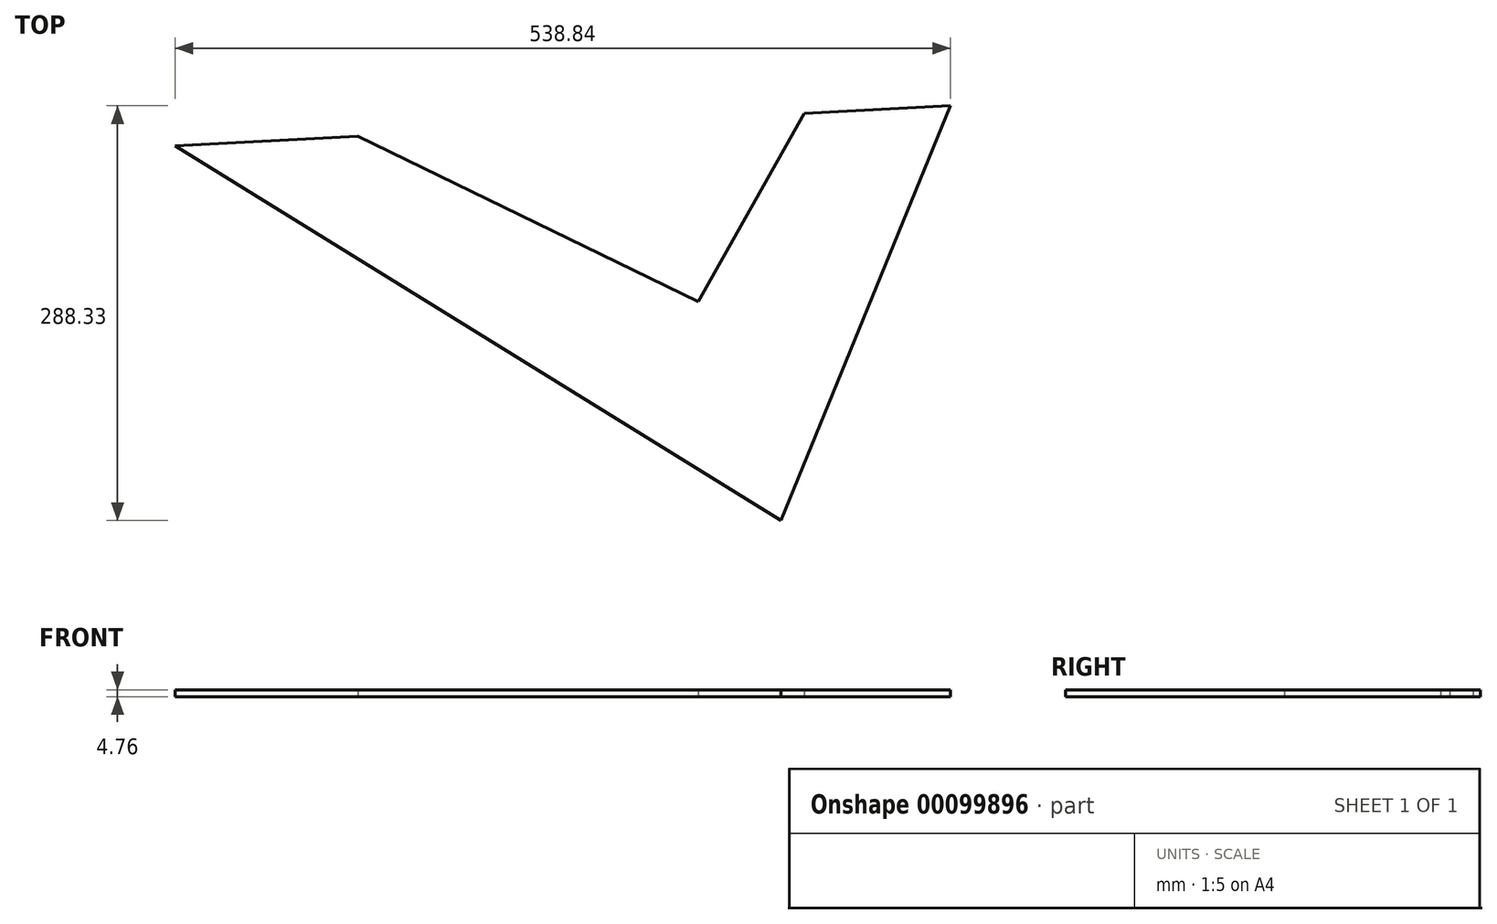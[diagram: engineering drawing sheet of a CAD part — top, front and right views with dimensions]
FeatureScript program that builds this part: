
annotation { "Feature Type Name" : "Feature", "Feature Type Description" : "" }
export const myFeature = defineFeature(function(context is Context, id is Id, definition is map)
    precondition{}
    {
        {
            var Q0;
            Q0=qCreatedBy(makeId("Top.planeOp"),FACE);
            var sketch = newSketch(context, id + "F0", { "sketchPlane" : qUnion([Q0])});
            skLineSegment(sketch, "E0", {"start": v(0, 0) * mm, "end": v(-117.63, -288.33) * mm});
            skLineSegment(sketch, "E1", {"start": v(-117.63, -288.33) * mm, "end": v(-538.84, -27.75) * mm});
            skLineSegment(sketch, "E2", {"start": v(-538.84, -27.75) * mm, "end": v(-411.84, -21.21) * mm});
            skLineSegment(sketch, "E3", {"start": v(-411.84, -21.21) * mm, "end": v(-175.25, -136.2) * mm});
            skLineSegment(sketch, "E4", {"start": v(-175.25, -136.2) * mm, "end": v(-101.6, -5.23) * mm});
            skLineSegment(sketch, "E5.trimOffspring", {"start": v(-101.6, -5.23) * mm, "end": v(0, 0) * mm});
            skSolve(sketch);
        }
        {
            var Q0;
            Q0 = qSketchRegion(id + "F0", true);
            extrude(context, id + "F1", {"entities" : qUnion([Q0]), "depth" : 4.76 * mm});
        }
    });
